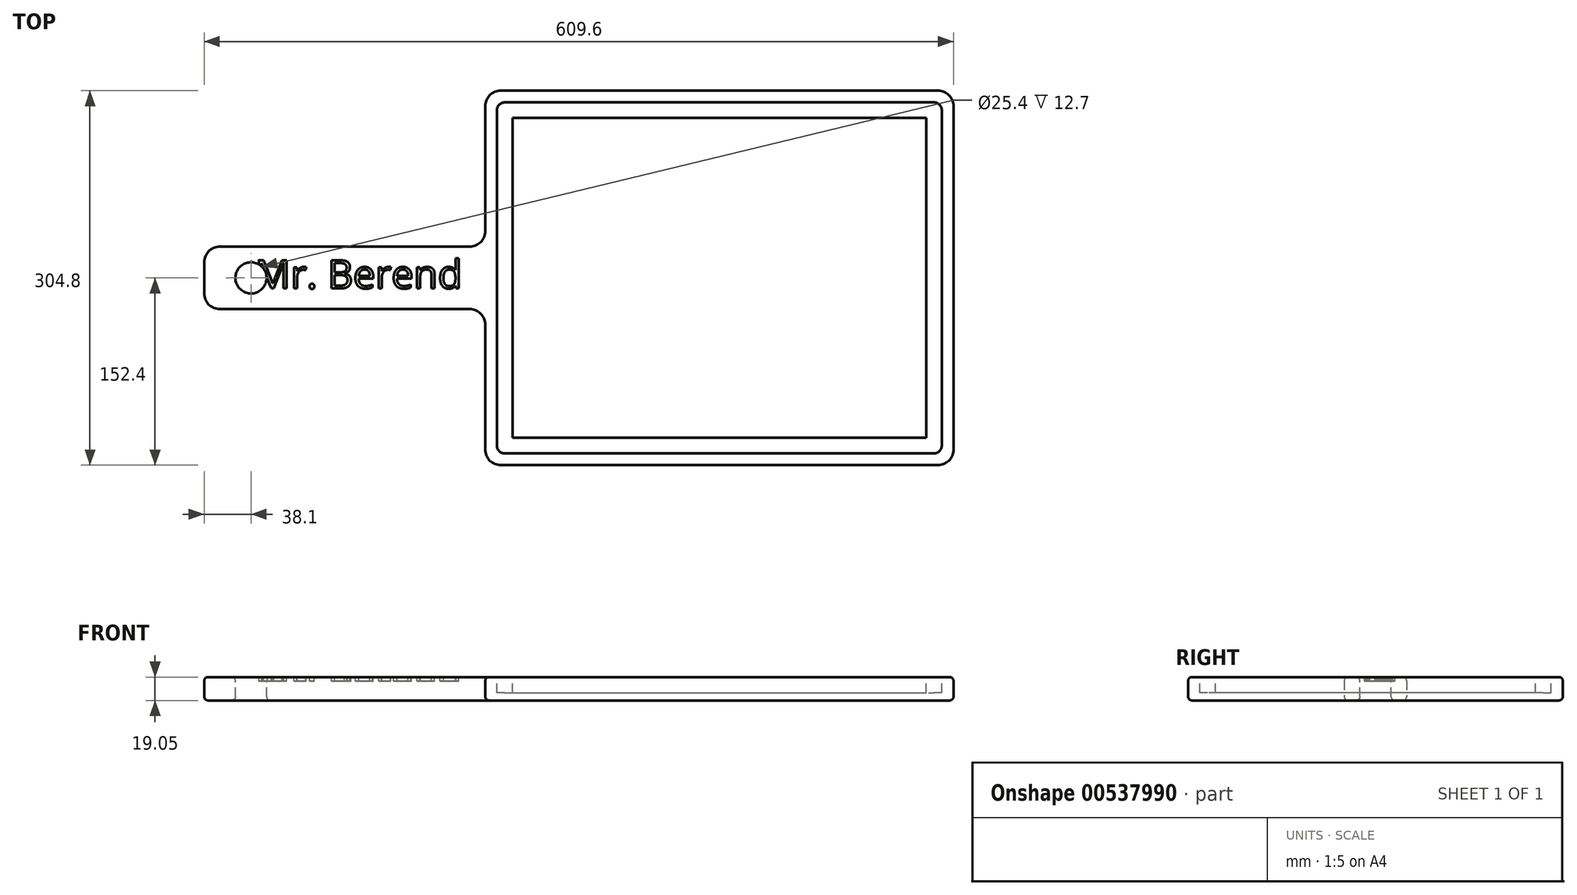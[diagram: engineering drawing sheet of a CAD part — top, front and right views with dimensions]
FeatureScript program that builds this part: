
annotation { "Feature Type Name" : "Feature", "Feature Type Description" : "" }
export const myFeature = defineFeature(function(context is Context, id is Id, definition is map)
    precondition{}
    {
        {
            var Q0;
            Q0=qCreatedBy(makeId("Top.planeOp"),FACE);
            var sketch = newSketch(context, id + "F0", { "sketchPlane" : qUnion([Q0])});
            skLineSegment(sketch, "E0.bottom", {"start": v(0, 0) * mm, "end": v(381, 0) * mm});
            skLineSegment(sketch, "E0.top", {"start": v(0, 304.8) * mm, "end": v(381, 304.8) * mm});
            skLineSegment(sketch, "E0.left", {"start": v(0, 0) * mm, "end": v(0, 304.8) * mm});
            skLineSegment(sketch, "E0.right", {"start": v(381, 0) * mm, "end": v(381, 304.8) * mm});
            skLineSegment(sketch, "E1.bottom", {"start": v(0, 177.8) * mm, "end": v(-228.6, 177.8) * mm});
            skLineSegment(sketch, "E1.top", {"start": v(0, 127) * mm, "end": v(-228.6, 127) * mm});
            skLineSegment(sketch, "E1.left", {"start": v(0, 177.8) * mm, "end": v(0, 127) * mm});
            skLineSegment(sketch, "E1.right", {"start": v(-228.6, 177.8) * mm, "end": v(-228.6, 127) * mm});
            skSolve(sketch);
        }
        {
            var Q0;
            {var subQ3=sQuery(id+"F0.wireOp",EDGE,"E0.bottom");Q0=makeQuery(id+"F0.imprint","IMPRINT",FACE,{"disambiguationData":[TD([[makeQuery(id+"F0.imprint","IMPRINT",EDGE,{"derivedFrom":subQ3}),1.0]])]});}
            var Q1;
            Q1=makeQuery(id+"F0.imprint","IMPRINT",FACE,{"disambiguationData":[TD([[makeQuery(id+"F0.imprint","IMPRINT",EDGE,{"derivedFrom":sQuery(id+"F0.wireOp",EDGE,"E1.bottom")}),1.0]])]});
            extrude(context, id + "F1", {"entities" : qUnion([Q0, Q1]), "depth" : 19.05 * mm, "offsetDistance" : 25.4 * mm});
        }
        {
            var Q0;
            Q0=makeQuery(id+"F1.opExtrude","CAP_FACE",FACE,{"disambiguationData":[OSD([sQuery(id+"F0.wireOp",EDGE,"E0.bottom"),sQuery(id+"F0.wireOp",EDGE,"E0.top"),sQuery(id+"F0.wireOp",EDGE,"E0.left"),sQuery(id+"F0.wireOp",EDGE,"E0.right"),sQuery(id+"F0.wireOp",EDGE,"E1.bottom"),sQuery(id+"F0.wireOp",EDGE,"E1.top"),sQuery(id+"F0.wireOp",EDGE,"E1.right")])],"isStart":false});
            var sketch = newSketch(context, id + "F2", { "sketchPlane" : qUnion([Q0])});
            skCircle(sketch, "E2", {"center": v(-190.5, 152.4) * mm, "radius": 12.7 * mm});
            skSolve(sketch);
        }
        {
            var Q0;
            Q0=makeQuery(id+"F2.imprint","IMPRINT",FACE,{"disambiguationData":[TD([[makeQuery(id+"F2.imprint","IMPRINT",EDGE,{"derivedFrom":sQuery(id+"F2.wireOp",EDGE,"E2")}),1.0]])]});
            extrude(context, id + "F3", {"entities" : qUnion([Q0]), "operationType" : NewBodyOperationType.REMOVE, "oppositeDirection" : true, "depth" : 25.4 * mm, "offsetDistance" : 25.4 * mm});
        }
        {
            var Q0;
            Q0=makeQuery(id+"F1.opExtrude","CAP_FACE",FACE,{"disambiguationData":[OSD([sQuery(id+"F0.wireOp",EDGE,"E0.bottom"),sQuery(id+"F0.wireOp",EDGE,"E0.top"),sQuery(id+"F0.wireOp",EDGE,"E0.left"),sQuery(id+"F0.wireOp",EDGE,"E0.right"),sQuery(id+"F0.wireOp",EDGE,"E1.bottom"),sQuery(id+"F0.wireOp",EDGE,"E1.top"),sQuery(id+"F0.wireOp",EDGE,"E1.right")])],"isStart":false});
            var sketch = newSketch(context, id + "F4", { "sketchPlane" : qUnion([Q0])});
            skLineSegment(sketch, "E3.0", {"start": v(0, 292.1) * mm, "end": v(381, 292.1) * mm});
            skLineSegment(sketch, "E4.0", {"start": v(0, 12.7) * mm, "end": v(381, 12.7) * mm});
            skLineSegment(sketch, "E5.0", {"start": v(12.7, 0) * mm, "end": v(12.7, 127) * mm});
            skLineSegment(sketch, "E6.0", {"start": v(12.7, 177.8) * mm, "end": v(12.7, 304.8) * mm});
            skLineSegment(sketch, "E7", {"start": v(12.7, 177.8) * mm, "end": v(12.7, 127) * mm});
            skSolve(sketch);
        }
        {
            var Q0;
            Q0=makeQuery(id+"F1.opExtrude","SWEPT_EDGE",EDGE,{"disambiguationData":[OSD([sQuery(id+"F0.wireOp",EDGE,"E1.top"),sQuery(id+"F0.wireOp",EDGE,"E1.right")])]});
            var Q1;
            Q1=makeQuery(id+"F1.opExtrude","SWEPT_EDGE",EDGE,{"disambiguationData":[OSD([sQuery(id+"F0.wireOp",EDGE,"E0.left"),sQuery(id+"F0.wireOp",EDGE,"E1.top"),sQuery(id+"F0.wireOp",EDGE,"E1.left")])]});
            var Q2;
            Q2=makeQuery(id+"F1.opExtrude","SWEPT_EDGE",EDGE,{"disambiguationData":[OSD([sQuery(id+"F0.wireOp",EDGE,"E0.bottom"),sQuery(id+"F0.wireOp",EDGE,"E0.left")])]});
            var Q3;
            Q3=makeQuery(id+"F1.opExtrude","SWEPT_EDGE",EDGE,{"disambiguationData":[OSD([sQuery(id+"F0.wireOp",EDGE,"E0.bottom"),sQuery(id+"F0.wireOp",EDGE,"E0.right")])]});
            var Q4;
            Q4=makeQuery(id+"F1.opExtrude","SWEPT_EDGE",EDGE,{"disambiguationData":[OSD([sQuery(id+"F0.wireOp",EDGE,"E0.top"),sQuery(id+"F0.wireOp",EDGE,"E0.right")])]});
            var Q5;
            Q5=makeQuery(id+"F1.opExtrude","SWEPT_EDGE",EDGE,{"disambiguationData":[OSD([sQuery(id+"F0.wireOp",EDGE,"E0.top"),sQuery(id+"F0.wireOp",EDGE,"E0.left")])]});
            var Q6;
            Q6=makeQuery(id+"F1.opExtrude","SWEPT_EDGE",EDGE,{"disambiguationData":[OSD([sQuery(id+"F0.wireOp",EDGE,"E0.left"),sQuery(id+"F0.wireOp",EDGE,"E1.bottom"),sQuery(id+"F0.wireOp",EDGE,"E1.left")])]});
            var Q7;
            Q7=makeQuery(id+"F1.opExtrude","SWEPT_EDGE",EDGE,{"disambiguationData":[OSD([sQuery(id+"F0.wireOp",EDGE,"E1.bottom"),sQuery(id+"F0.wireOp",EDGE,"E1.right")])]});
            fillet(context, id + "F5", {"entities" : qUnion([Q0, Q1, Q2, Q3, Q4, Q5, Q6, Q7]), "radius" : 12.7 * mm, "tangentPropagation" : true, "allowEdgeOverflow" : false});
        }
        {
            var Q0;
            Q0=makeQuery(id+"F1.opExtrude","CAP_FACE",FACE,{"disambiguationData":[OSD([sQuery(id+"F0.wireOp",EDGE,"E0.bottom"),sQuery(id+"F0.wireOp",EDGE,"E0.top"),sQuery(id+"F0.wireOp",EDGE,"E0.left"),sQuery(id+"F0.wireOp",EDGE,"E0.right"),sQuery(id+"F0.wireOp",EDGE,"E1.bottom"),sQuery(id+"F0.wireOp",EDGE,"E1.top"),sQuery(id+"F0.wireOp",EDGE,"E1.right")])],"isStart":false});
            var Q1;
            Q1=makeQuery(id+"F1.opExtrude","CAP_FACE",FACE,{"disambiguationData":[OSD([sQuery(id+"F0.wireOp",EDGE,"E0.bottom"),sQuery(id+"F0.wireOp",EDGE,"E0.top"),sQuery(id+"F0.wireOp",EDGE,"E0.left"),sQuery(id+"F0.wireOp",EDGE,"E0.right"),sQuery(id+"F0.wireOp",EDGE,"E1.bottom"),sQuery(id+"F0.wireOp",EDGE,"E1.top"),sQuery(id+"F0.wireOp",EDGE,"E1.right")])],"isStart":true});
            fillet(context, id + "F6", {"entities" : qUnion([Q0, Q1]), "radius" : 3.17 * mm, "tangentPropagation" : true, "allowEdgeOverflow" : false});
        }
        {
            var Q0;
            {var subQ0=sQuery(id+"F4.wireOp",EDGE,"E7");Q0=makeQuery(id+"F4.imprint","IMPRINT",FACE,{"disambiguationData":[TD([[makeQuery(id+"F4.imprint","IMPRINT",EDGE,{"derivedFrom":subQ0}),1.0]])]});}
            var sketch = newSketch(context, id + "F7", { "sketchPlane" : qUnion([Q0])});
            skLineSegment(sketch, "E8.bottom", {"start": v(15.87, 295.28) * mm, "end": v(365.13, 295.28) * mm});
            skLineSegment(sketch, "E8.top", {"start": v(15.88, 9.53) * mm, "end": v(365.13, 9.53) * mm});
            skLineSegment(sketch, "E8.left", {"start": v(9.52, 288.93) * mm, "end": v(9.53, 15.88) * mm});
            skLineSegment(sketch, "E8.right", {"start": v(371.48, 288.93) * mm, "end": v(371.48, 15.88) * mm});
            skPoint(sketch, "E9.visualSharp", {"position": v(9.52, 295.28) * mm});
            skArc(sketch, "E9.filletArc", {"start": v(15.87, 295.28) * mm, "mid": v(11.38, 293.42) * mm, "end": v(9.53, 288.93) * mm});
            skPoint(sketch, "E10.visualSharp", {"position": v(371.48, 295.28) * mm});
            skArc(sketch, "E10.filletArc", {"start": v(371.48, 288.93) * mm, "mid": v(369.62, 293.42) * mm, "end": v(365.13, 295.28) * mm});
            skPoint(sketch, "E11.visualSharp", {"position": v(371.48, 9.53) * mm});
            skArc(sketch, "E11.filletArc", {"start": v(365.13, 9.53) * mm, "mid": v(369.62, 11.38) * mm, "end": v(371.48, 15.88) * mm});
            skPoint(sketch, "E12.visualSharp", {"position": v(9.53, 9.53) * mm});
            skArc(sketch, "E12.filletArc", {"start": v(9.53, 15.88) * mm, "mid": v(11.38, 11.38) * mm, "end": v(15.88, 9.53) * mm});
            skLineSegment(sketch, "E13.0", {"start": v(22.22, 282.58) * mm, "end": v(358.78, 282.58) * mm});
            skLineSegment(sketch, "E13.1", {"start": v(22.22, 282.58) * mm, "end": v(22.22, 22.22) * mm});
            skLineSegment(sketch, "E13.2", {"start": v(22.22, 22.23) * mm, "end": v(358.78, 22.23) * mm});
            skLineSegment(sketch, "E13.3", {"start": v(358.78, 282.58) * mm, "end": v(358.78, 22.22) * mm});
            skSolve(sketch);
        }
        {
            var Q0;
            Q0 = qSketchRegion(id + "F7", true);
            extrude(context, id + "F8", {"entities" : qUnion([Q0]), "operationType" : NewBodyOperationType.REMOVE, "oppositeDirection" : true, "depth" : 12.7 * mm, "offsetDistance" : 25.4 * mm});
        }
        {
            var Q0;
            {var subQ9=sQuery(id+"F4.wireOp",EDGE,"E7");Q0=makeQuery(id+"F4.imprint","IMPRINT",FACE,{"disambiguationData":[TD([[makeQuery(id+"F4.imprint","IMPRINT",EDGE,{"derivedFrom":subQ9}),-1.0]])]});}
            var sketch = newSketch(context, id + "F9", { "sketchPlane" : qUnion([Q0])});
            skText(sketch, "E14", { "text": "Mr. Berend", "fontName": "OpenSans-Regular.ttf"});
            const initialGuessF9  = {"E14": [-0.18733, 0.14386, 1, 0, 0.02315]};
            skSetInitialGuess(sketch, initialGuessF9);
            skSolve(sketch);
        }
        {
            var Q0;
            Q0 = qSketchRegion(id + "F9", true);
            extrude(context, id + "F10", {"entities" : qUnion([Q0]), "operationType" : NewBodyOperationType.REMOVE, "oppositeDirection" : true, "depth" : 3.17 * mm, "offsetDistance" : 25.4 * mm});
        }
    });
